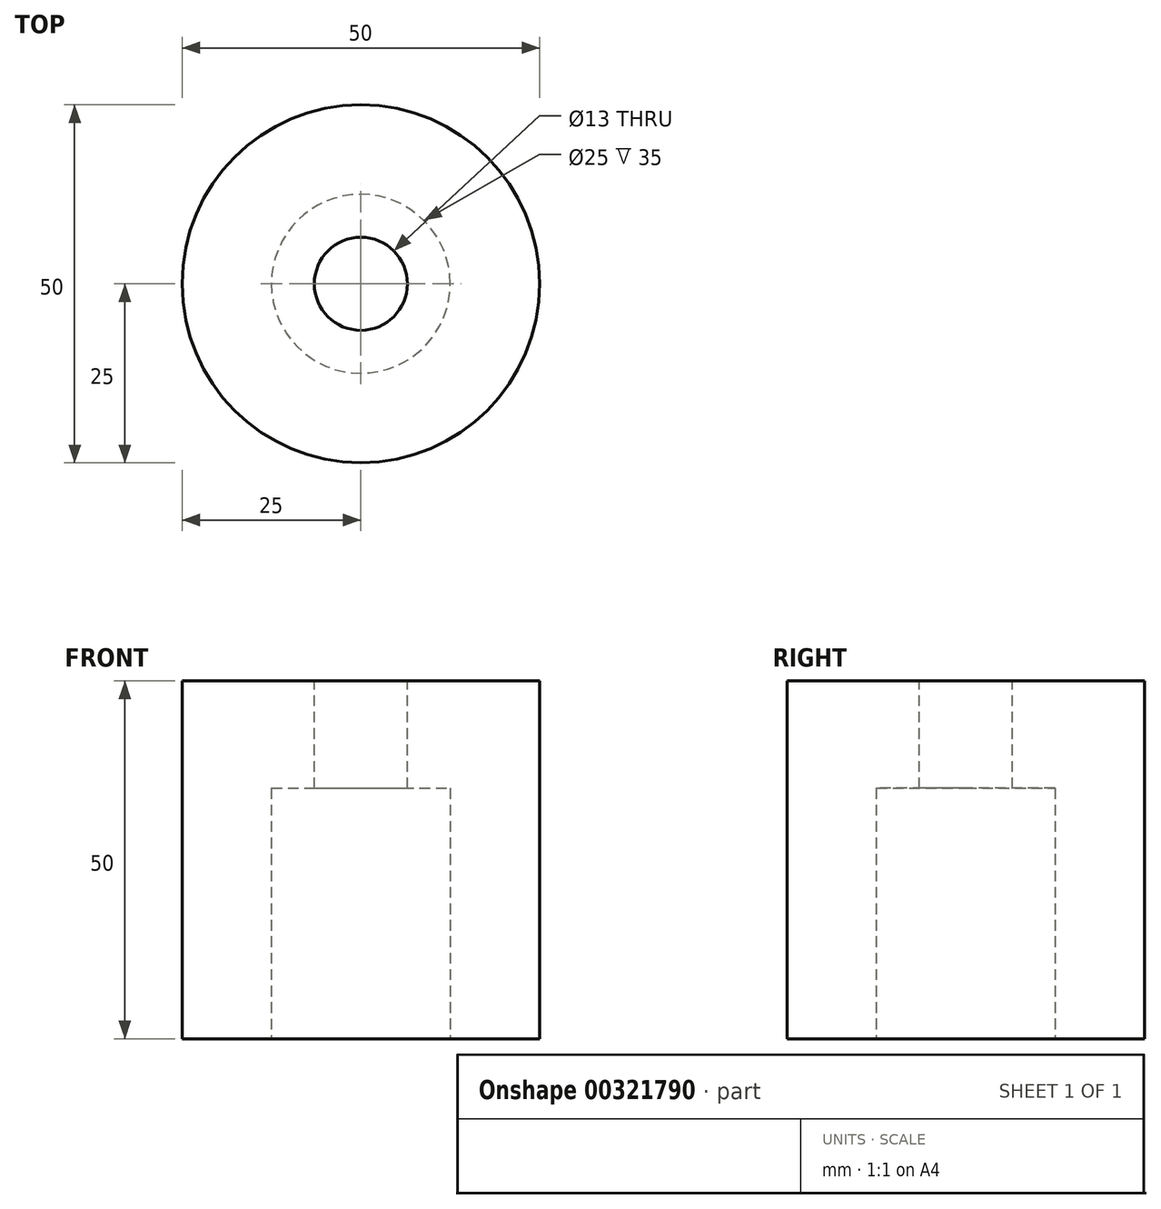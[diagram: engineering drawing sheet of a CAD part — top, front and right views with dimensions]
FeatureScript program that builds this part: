
annotation { "Feature Type Name" : "Feature", "Feature Type Description" : "" }
export const myFeature = defineFeature(function(context is Context, id is Id, definition is map)
    precondition{}
    {
        {
            var Q0;
            Q0=qCreatedBy(makeId("Top.planeOp"),FACE);
            var sketch = newSketch(context, id + "F0", { "sketchPlane" : qUnion([Q0])});
            skCircle(sketch, "E0", {"center": v(0, 0) * mm, "radius": 25 * mm});
            skSolve(sketch);
        }
        {
            var Q0;
            Q0=makeQuery(id+"F0.imprint","IMPRINT",FACE,{"disambiguationData":[TD([[makeQuery(id+"F0.imprint","IMPRINT",EDGE,{"derivedFrom":sQuery(id+"F0.wireOp",EDGE,"E0")}),1.0]])]});
            extrude(context, id + "F1", {"entities" : qUnion([Q0]), "depth" : 50 * mm});
        }
        {
            var Q0;
            Q0=makeQuery(id+"F1.opExtrude","CAP_FACE",FACE,{"disambiguationData":[OSD([sQuery(id+"F0.wireOp",EDGE,"E0")])],"isStart":false});
            var sketch = newSketch(context, id + "F2", { "sketchPlane" : qUnion([Q0])});
            skCircle(sketch, "E1", {"center": v(0, 0) * mm, "radius": 6.5 * mm});
            skSolve(sketch);
        }
        {
            var Q0;
            Q0=makeQuery(id+"F2.imprint","IMPRINT",FACE,{"disambiguationData":[TD([[makeQuery(id+"F2.imprint","IMPRINT",EDGE,{"derivedFrom":sQuery(id+"F2.wireOp",EDGE,"E1")}),1.0]])]});
            extrude(context, id + "F3", {"entities" : qUnion([Q0]), "operationType" : NewBodyOperationType.REMOVE, "oppositeDirection" : true, "depth" : 50 * mm});
        }
        {
            var Q0;
            Q0=makeQuery(id+"F1.opExtrude","CAP_FACE",FACE,{"disambiguationData":[OSD([sQuery(id+"F0.wireOp",EDGE,"E0")])],"isStart":true});
            var sketch = newSketch(context, id + "F4", { "sketchPlane" : qUnion([Q0])});
            skCircle(sketch, "E2", {"center": v(0, 0) * mm, "radius": 12.5 * mm});
            skSolve(sketch);
        }
        {
            var Q0;
            Q0 = qSketchRegion(id + "F4", true);
            extrude(context, id + "F5", {"entities" : qUnion([Q0]), "operationType" : NewBodyOperationType.REMOVE, "oppositeDirection" : true, "depth" : 35 * mm});
        }
    });
